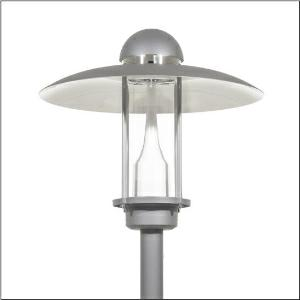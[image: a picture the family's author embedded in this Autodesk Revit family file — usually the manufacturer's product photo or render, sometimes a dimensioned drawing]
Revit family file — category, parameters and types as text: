
# Revit family: city-light_elegance_iq___p1_0a_5xa5265nf14h_5982
name_source: partatom
category: Lighting Fixtures
units: mm (PartAtom-declared; Revit-internal decimal feet)

## family parameters
Cut with Voids When Loaded = No
Host = Face
Light Source = No
Part Type = Normal
Room Calculation Point = No
Round Connector Dimension = Use Diameter
Shared = No

## types (1)
- --- (1 x LED, 1440 lm, 11.8 W, 2700K)
    Apparent Load = 12 VA
    CIE Flux Codes = 32 62 91 97 100
    Color Rendering = 70
    Color Temperature = 2700K
    Default Elevation = 1800 mm
    Description = City-Light Elegance iQ, mast luminaire, Module 540 iQ-SR, primary light control with 3 zone facetted reflector, of plastic, silver coated, highly specular, structured, primary optical cover: cover, of PMMA, transparent, light distribution: P1.0a, light emission: direct distribution, primary light characteristic: strongly asymmetric, installation type: post-top, LED, High Power LED, rated luminous flux: 1.440lm, luminous efficacy: 122lm/W, light colour: 727, colour temperature: 2700K, control gear: ECG iQ, control: pre-setting: logarithmic dimming characteristic, Street-Remote, Auto-Match, Temp-Guard, Lumen-Switch, Night-Set, Smart-Wire, Light-Fading, Desk-Remote (wireless, voltage-free reading and setting of iQ features in the workshop via application-optimized NFC function/RFID function), optimised constant luminous flux control (CLO 2.0), with terminal, 6-pole, max. 2.5mm², mains connection: 230..240V, AC, 50/60Hz, start of lifetime: 12W, end of service life: 12W, reduction: 6W, luminaire housing, upper part, of aluminium, coated, Siteco® metallic grey (DB 702S), diameter: 750mm, height: 675mm, spigot size: d x l = 76 x 70mm (post-top) | with reducer (optional accessory) 60 x 70mm, post-top mast mounting element, of diecast aluminium, coated, Siteco® metallic grey (DB 702S), Module 540 iQ-SR, traffic white (RAL 9016), equipment: standard, protection rating (complete): IP65, insulation class (complete): insulation class II (safety insulation), certification: CE, ENEC, VDE, packaging unit: 1 piece

Light Distribution: P1.0a
    Height = 675 mm
    Lamp = 1 x LED
    Lamp Light Flux = 1440 lm
    Lamp Power = 11.8 W
    Lamp count = 1
    Length = 750 mm
    Luminous efficacy = 122 lm/W
    Manufacturer = Siteco
    ModVariant = No
    Model = 5XA5265NF14H
    Number of Poles = 1
    OnlyDefault = Yes
    Power Factor = 1
    Product Name = City-Light Elegance iQ | P1.0a
    Product group = mast luminaire | pylon top
    ProductGroupID = 6100
    Protection Class = Protection class II
    Protection Degree = IP 65
    RLX_Detail_Level = 1
    RLX_Emergency_Light_Flux = 0 lm
    RLX_Emergency_Type = 0
    RLX_Emergency_Type_DB = No
    RlxData = <blob elided: 101797 chars, md5=bd7702ef>
    Socket = socket
    Standby Power = 0 W
    System Light Flux = 1440 lm
    System Power = 12 W
    Type Comments = factory setting: luminous flux: 100 % | dim-lin: 254 | 472 mA
    Type Image = l_1006912.jpg
    URL = http://relux.com
    VarID = @adj_123587
    Voltage = 0 V
    Weight = 0.00 kg
    Width = 0 mm  [stored 0 ft]

note: [stored X ft] marks values corroborated as IEEE doubles in the binary element streams (Revit-internal decimal feet)

## geometry (parser evidence)
native form markers: Blend x4, Sweep x9
no freeform markers — native parametric forms only
